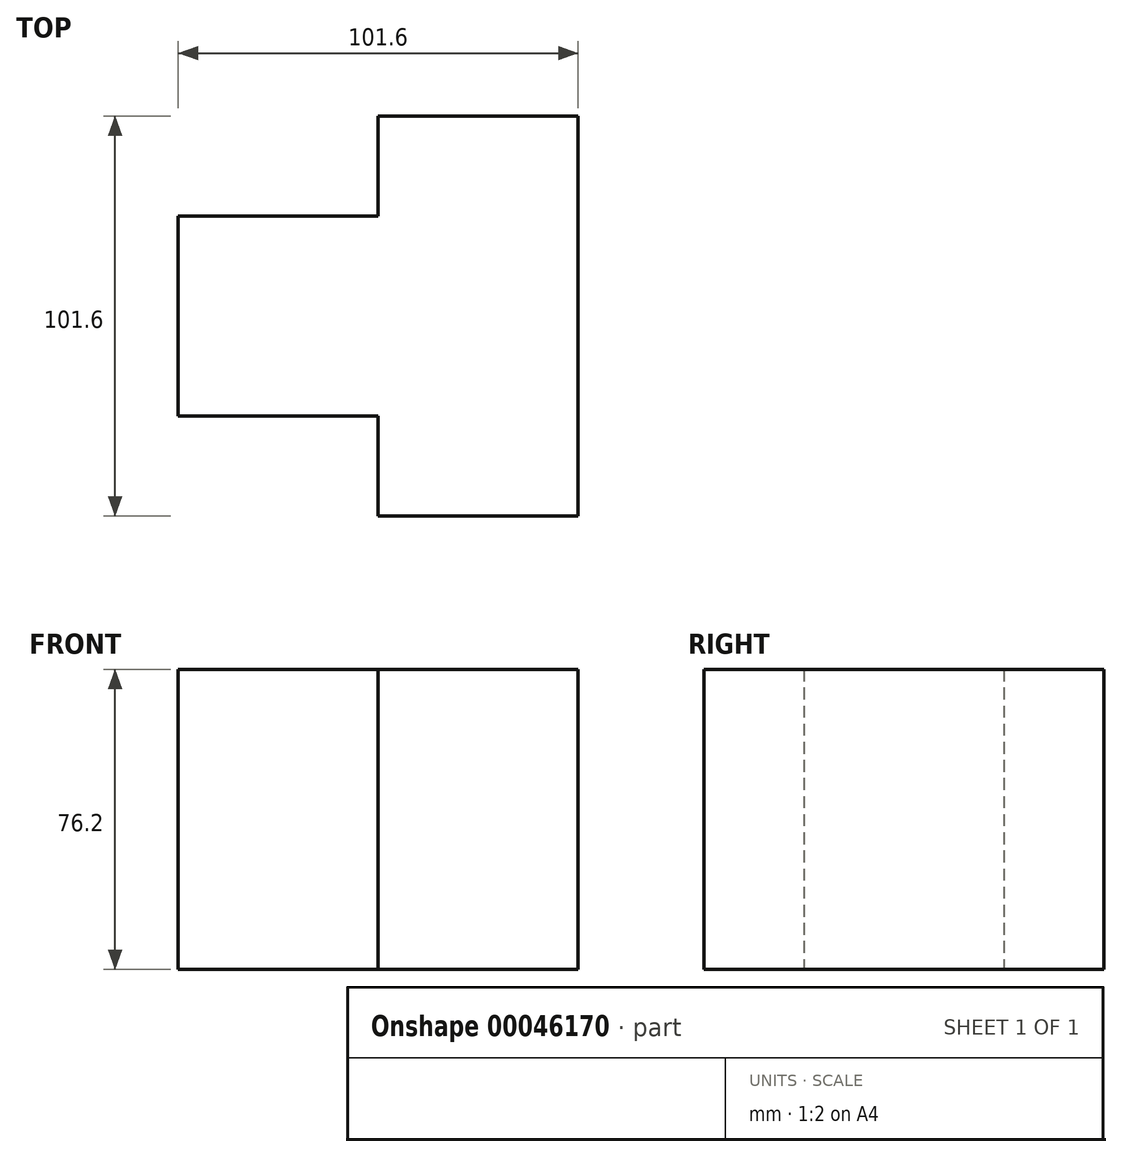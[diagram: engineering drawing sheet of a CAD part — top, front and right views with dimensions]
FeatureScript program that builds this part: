
annotation { "Feature Type Name" : "Feature", "Feature Type Description" : "" }
export const myFeature = defineFeature(function(context is Context, id is Id, definition is map)
    precondition{}
    {
        {
            var Q0;
            Q0=qCreatedBy(makeId("Top.planeOp"),FACE);
            var sketch = newSketch(context, id + "F0", { "sketchPlane" : qUnion([Q0])});
            skLineSegment(sketch, "E0.top", {"start": v(0, 50.8) * mm, "end": v(50.8, 50.8) * mm});
            skLineSegment(sketch, "E0.right", {"start": v(50.8, 0) * mm, "end": v(50.8, 50.8) * mm});
            skLineSegment(sketch, "E1.top", {"start": v(0, -50.8) * mm, "end": v(50.8, -50.8) * mm});
            skLineSegment(sketch, "E1.right", {"start": v(50.8, 0) * mm, "end": v(50.8, -50.8) * mm});
            skLineSegment(sketch, "E2.bottom", {"start": v(0, -25.4) * mm, "end": v(-50.8, -25.4) * mm});
            skLineSegment(sketch, "E2.top", {"start": v(0, 25.4) * mm, "end": v(-50.8, 25.4) * mm});
            skLineSegment(sketch, "E2.right", {"start": v(-50.8, -25.4) * mm, "end": v(-50.8, 25.4) * mm});
            skPoint(sketch, "E0.bottom.start.orphan", {"position": v(0, 0) * mm});
            skLineSegment(sketch, "E3", {"start": v(0, 25.4) * mm, "end": v(0, 50.8) * mm});
            skLineSegment(sketch, "E4", {"start": v(0, -50.8) * mm, "end": v(0, -25.4) * mm});
            skSolve(sketch);
        }
        {
            var Q0;
            Q0=makeQuery(id+"F0.imprint","IMPRINT",FACE,{"disambiguationData":[TD([[makeQuery(id+"F0.imprint","IMPRINT",EDGE,{"derivedFrom":sQuery(id+"F0.wireOp",EDGE,"E0.top")}),-1.0]])]});
            extrude(context, id + "F1", {"entities" : qUnion([Q0]), "depth" : 76.2 * mm});
        }
    });
